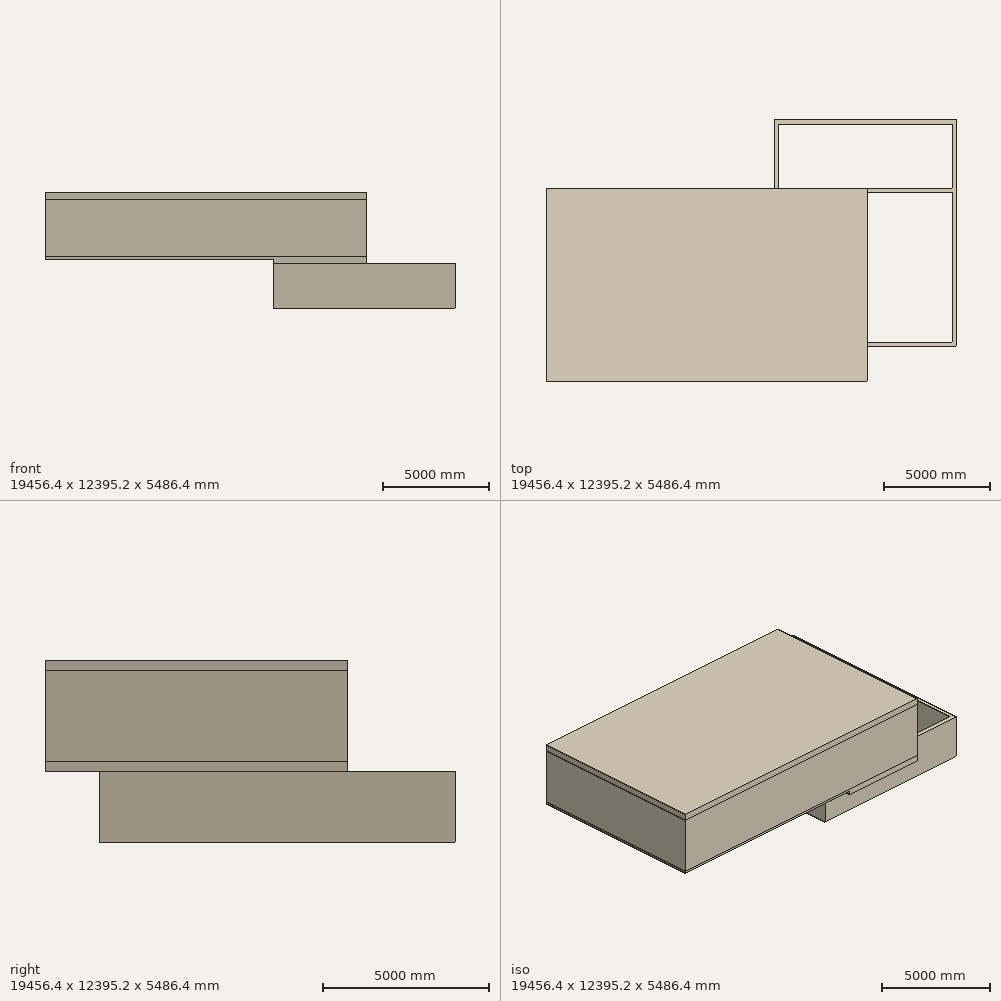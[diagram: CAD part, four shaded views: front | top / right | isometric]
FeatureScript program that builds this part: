
annotation { "Feature Type Name" : "Feature", "Feature Type Description" : "" }
export const myFeature = defineFeature(function(context is Context, id is Id, definition is map)
    precondition{}
    {
        {
            var Q0;
            Q0=qCreatedBy(makeId("Top.planeOp"),FACE);
            var sketch = newSketch(context, id + "F0", { "sketchPlane" : qUnion([Q0])});
            skLineSegment(sketch, "E0.bottom", {"start": v(4318, -5384.8) * mm, "end": v(-4318, -5384.8) * mm});
            skLineSegment(sketch, "E0.top", {"start": v(4318, 5384.8) * mm, "end": v(-4318, 5384.8) * mm});
            skLineSegment(sketch, "E0.left", {"start": v(4318, -5384.8) * mm, "end": v(4318, 5384.8) * mm});
            skLineSegment(sketch, "E0.right", {"start": v(-4318, -5384.8) * mm, "end": v(-4318, 5384.8) * mm});
            skPoint(sketch, "E0.middle", {"position": v(0, 0) * mm});
            skLineSegment(sketch, "E1.bottom", {"start": v(4114.8, -5181.6) * mm, "end": v(-4114.8, -5181.6) * mm});
            skLineSegment(sketch, "E1.top", {"start": v(4114.8, 5181.6) * mm, "end": v(-4114.8, 5181.6) * mm});
            skLineSegment(sketch, "E1.left", {"start": v(4114.8, -5181.6) * mm, "end": v(4114.8, 5181.6) * mm});
            skLineSegment(sketch, "E1.right", {"start": v(-4114.8, -5181.6) * mm, "end": v(-4114.8, 5181.6) * mm});
            skLineSegment(sketch, "E2.bottom", {"start": v(-4114.8, 2133.6) * mm, "end": v(1168.4, 2133.6) * mm});
            skLineSegment(sketch, "E2.top", {"start": v(-4114.8, 1930.4) * mm, "end": v(1168.4, 1930.4) * mm});
            skLineSegment(sketch, "E2.left", {"start": v(-4114.8, 2133.6) * mm, "end": v(-4114.8, 1930.4) * mm});
            skLineSegment(sketch, "E2.right", {"start": v(1168.4, 2133.6) * mm, "end": v(1168.4, 1930.4) * mm});
            skLineSegment(sketch, "E3.bottom", {"start": v(4114.8, 2133.6) * mm, "end": v(3302, 2133.6) * mm});
            skLineSegment(sketch, "E3.top", {"start": v(4114.8, 1930.4) * mm, "end": v(3302, 1930.4) * mm});
            skLineSegment(sketch, "E3.left", {"start": v(4114.8, 2133.6) * mm, "end": v(4114.8, 1930.4) * mm});
            skLineSegment(sketch, "E3.right", {"start": v(3302, 2133.6) * mm, "end": v(3302, 1930.4) * mm});
            skLineSegment(sketch, "E4.bottom", {"start": v(101.6, 1930.4) * mm, "end": v(-101.6, 1930.4) * mm});
            skLineSegment(sketch, "E4.top", {"start": v(101.6, -5181.6) * mm, "end": v(-101.6, -5181.6) * mm});
            skLineSegment(sketch, "E4.left", {"start": v(101.6, 1930.4) * mm, "end": v(101.6, -5181.6) * mm});
            skLineSegment(sketch, "E4.right", {"start": v(-101.6, 1930.4) * mm, "end": v(-101.6, -5181.6) * mm});
            skSolve(sketch);
        }
        {
            var Q0;
            Q0=makeQuery(id+"F0.imprint","IMPRINT",FACE,{"disambiguationData":[TD([[makeQuery(id+"F0.imprint","IMPRINT",EDGE,{"derivedFrom":sQuery(id+"F0.wireOp",EDGE,"E0.bottom")}),-1.0]])]});
            var Q1;
            {var subQ6=sQuery(id+"F0.wireOp",EDGE,"E2.bottom");Q1=makeQuery(id+"F0.imprint","IMPRINT",FACE,{"disambiguationData":[TD([[makeQuery(id+"F0.imprint","IMPRINT",EDGE,{"derivedFrom":subQ6}),-1.0]])]});}
            var Q2;
            {var subQ2=sQuery(id+"F0.wireOp",EDGE,"E4.left");Q2=makeQuery(id+"F0.imprint","IMPRINT",FACE,{"disambiguationData":[TD([[makeQuery(id+"F0.imprint","IMPRINT",EDGE,{"derivedFrom":subQ2}),-1.0]])]});}
            var Q3;
            {var subQ0=sQuery(id+"F0.wireOp",EDGE,"E3.bottom");Q3=makeQuery(id+"F0.imprint","IMPRINT",FACE,{"disambiguationData":[TD([[makeQuery(id+"F0.imprint","IMPRINT",EDGE,{"derivedFrom":subQ0}),1.0]])]});}
            extrude(context, id + "F1", {"entities" : qUnion([Q0, Q1, Q2, Q3]), "depth" : 2133.6 * mm, "offsetDistance" : 30.48 * mm});
        }
        {
            var Q0;
            {var subQ0=sQuery(id+"F0.wireOp",EDGE,"E2.top");Q0=makeQuery(id+"F1.opExtrude","SWEPT_FACE",FACE,{"disambiguationData":[OSD([subQ0]),TDD([makeQuery(id+"F0.imprint","IMPRINT",EDGE,{"disambiguationData":[TD([[makeQuery(id+"F0.imprint","INTERSECT",VERTEX,{"derivedFrom":[subQ0,sQuery(id+"F0.wireOp",EDGE,"E4.left")]}),-1.0]])],"derivedFrom":subQ0})])]});}
            var sketch = newSketch(context, id + "F2", { "sketchPlane" : qUnion([Q0])});
            skLineSegment(sketch, "E5", {"start": v(1168.4, 1930.4) * mm, "end": v(3302, 1930.4) * mm, "construction": true});
            skLineSegment(sketch, "E6", {"start": v(1168.4, 2133.6) * mm, "end": v(3302, 2133.6) * mm});
            skArc(sketch, "E7", {"start": v(2235.2, 1930.4) * mm, "mid": v(1548.93, 1687.44) * mm, "end": v(1168.4, 1066.8) * mm});
            skArc(sketch, "E8", {"start": v(3302, 1066.8) * mm, "mid": v(2921.47, 1687.44) * mm, "end": v(2235.2, 1930.4) * mm});
            skLineSegment(sketch, "E9", {"start": v(1168.4, 1066.8) * mm, "end": v(1168.4, 2133.6) * mm});
            skLineSegment(sketch, "E10", {"start": v(3302, 2133.6) * mm, "end": v(3302, 1066.8) * mm});
            skSolve(sketch);
        }
        {
            var Q0;
            Q0 = qSketchRegion(id + "F2", true);
            var Q1;
            Q1=makeQuery(id+"F1.opExtrude","SWEPT_FACE",FACE,{"disambiguationData":[OSD([sQuery(id+"F0.wireOp",EDGE,"E2.bottom")])]});
            extrude(context, id + "F3", {"entities" : qUnion([Q0]), "operationType" : NewBodyOperationType.ADD, "endBound" : BoundingType.UP_TO_SURFACE, "oppositeDirection" : true, "depth" : 30.48 * mm, "endBoundEntityFace" : qUnion([Q1]), "offsetDistance" : 30.48 * mm});
        }
        {
            var Q0;
            Q0=makeQuery(id+"F3.boolean.opBoolean","MERGE",FACE,{"derivedFrom":[makeQuery(id+"F1.opExtrude","CAP_FACE",FACE,{"disambiguationData":[OSD([sQuery(id+"F0.wireOp",EDGE,"E0.bottom"),sQuery(id+"F0.wireOp",EDGE,"E0.top"),sQuery(id+"F0.wireOp",EDGE,"E0.left"),sQuery(id+"F0.wireOp",EDGE,"E0.right"),sQuery(id+"F0.wireOp",EDGE,"E1.bottom"),sQuery(id+"F0.wireOp",EDGE,"E1.top"),sQuery(id+"F0.wireOp",EDGE,"E1.left"),sQuery(id+"F0.wireOp",EDGE,"E1.right"),sQuery(id+"F0.wireOp",EDGE,"E2.bottom"),sQuery(id+"F0.wireOp",EDGE,"E2.top"),sQuery(id+"F0.wireOp",EDGE,"E2.right"),sQuery(id+"F0.wireOp",EDGE,"E3.bottom"),sQuery(id+"F0.wireOp",EDGE,"E3.top"),sQuery(id+"F0.wireOp",EDGE,"E3.right"),sQuery(id+"F0.wireOp",EDGE,"E4.left"),sQuery(id+"F0.wireOp",EDGE,"E4.right")])],"isStart":false}),makeQuery(id+"F3.opExtrude","SWEPT_FACE",FACE,{"disambiguationData":[OSD([sQuery(id+"F2.wireOp",EDGE,"E6")])]})]});
            var sketch = newSketch(context, id + "F4", { "sketchPlane" : qUnion([Q0])});
            skLineSegment(sketch, "E11.bottom", {"start": v(101.6, -7010.4) * mm, "end": v(-4318, -7010.4) * mm});
            skLineSegment(sketch, "E11.top", {"start": v(101.6, 2133.6) * mm, "end": v(-4318, 2133.6) * mm});
            skLineSegment(sketch, "E11.left", {"start": v(101.6, -7010.4) * mm, "end": v(101.6, 2133.6) * mm});
            skLineSegment(sketch, "E11.right", {"start": v(-4318, -7010.4) * mm, "end": v(-4318, 2133.6) * mm});
            skSolve(sketch);
        }
        {
            var Q0;
            Q0 = qSketchRegion(id + "F4", true);
            extrude(context, id + "F5", {"entities" : qUnion([Q0]), "depth" : 304.8 * mm, "offsetDistance" : 30.48 * mm});
        }
        {
            var Q0;
            Q0=makeQuery(id+"F5.opExtrude","CAP_FACE",FACE,{"disambiguationData":[OSD([sQuery(id+"F4.wireOp",EDGE,"E11.bottom"),sQuery(id+"F4.wireOp",EDGE,"E11.top"),sQuery(id+"F4.wireOp",EDGE,"E11.left"),sQuery(id+"F4.wireOp",EDGE,"E11.right")])],"isStart":false});
            var sketch = newSketch(context, id + "F6", { "sketchPlane" : qUnion([Q0])});
            skLineSegment(sketch, "E12.bottom", {"start": v(-4318, -7010.4) * mm, "end": v(-15138.4, -7010.4) * mm});
            skLineSegment(sketch, "E12.top", {"start": v(-4318, 2133.6) * mm, "end": v(-15138.4, 2133.6) * mm});
            skLineSegment(sketch, "E12.left", {"start": v(-4318, -7010.4) * mm, "end": v(-4318, 2133.6) * mm});
            skLineSegment(sketch, "E12.right", {"start": v(-15138.4, -7010.4) * mm, "end": v(-15138.4, 2133.6) * mm});
            skSolve(sketch);
        }
        {
            var Q0;
            Q0 = qSketchRegion(id + "F6", true);
            var Q1;
            Q1=makeQuery(id+"F6.imprint","IMPRINT",FACE,{"disambiguationData":[TD([[makeQuery(id+"F6.imprint","IMPRINT",EDGE,{"derivedFrom":sQuery(id+"F6.wireOp",EDGE,"E12.left")}),-1.0]])]});
            extrude(context, id + "F7", {"entities" : qUnion([Q0, Q1]), "operationType" : NewBodyOperationType.ADD, "oppositeDirection" : true, "depth" : 127 * mm, "offsetDistance" : 30.48 * mm});
        }
        {
            var Q0;
            {var subQ0=sQuery(id+"F4.wireOp",EDGE,"E11.left");var subQ1=sQuery(id+"F4.wireOp",EDGE,"E11.top");var subQ2=sQuery(id+"F4.wireOp",EDGE,"E11.bottom");Q0=makeQuery(id+"F7.boolean.opBoolean","MERGE",FACE,{"derivedFrom":[makeQuery(id+"F5.opExtrude","CAP_FACE",FACE,{"disambiguationData":[OSD([subQ2,subQ1,subQ0,sQuery(id+"F4.wireOp",EDGE,"E11.right")])],"isStart":false}),makeQuery(id+"F7.opExtrude","CAP_FACE",FACE,{"disambiguationData":[OSD([subQ2,subQ1,subQ0,sQuery(id+"F6.wireOp",EDGE,"E12.bottom"),sQuery(id+"F6.wireOp",EDGE,"E12.top"),sQuery(id+"F6.wireOp",EDGE,"E12.right")])],"isStart":true})]});}
            var sketch = newSketch(context, id + "F8", { "sketchPlane" : qUnion([Q0])});
            skLineSegment(sketch, "E13.bottom", {"start": v(101.6, 2133.6) * mm, "end": v(-15138.4, 2133.6) * mm});
            skLineSegment(sketch, "E13.top", {"start": v(101.6, -7010.4) * mm, "end": v(-15138.4, -7010.4) * mm});
            skLineSegment(sketch, "E13.left", {"start": v(101.6, 2133.6) * mm, "end": v(101.6, -7010.4) * mm});
            skLineSegment(sketch, "E13.right", {"start": v(-15138.4, 2133.6) * mm, "end": v(-15138.4, -7010.4) * mm});
            skLineSegment(sketch, "E14.bottom", {"start": v(-101.6, 1930.4) * mm, "end": v(-14935.2, 1930.4) * mm});
            skLineSegment(sketch, "E14.top", {"start": v(-101.6, -6807.2) * mm, "end": v(-14935.2, -6807.2) * mm});
            skLineSegment(sketch, "E14.left", {"start": v(-101.6, 1930.4) * mm, "end": v(-101.6, -6807.2) * mm});
            skLineSegment(sketch, "E14.right", {"start": v(-14935.2, 1930.4) * mm, "end": v(-14935.2, -6807.2) * mm});
            skLineSegment(sketch, "E15.left", {"start": v(101.6, -1586.05) * mm, "end": v(101.6, -1312.76) * mm});
            skLineSegment(sketch, "E15.right", {"start": v(-101.6, -1586.05) * mm, "end": v(-101.6, -1312.76) * mm});
            skSolve(sketch);
        }
        {
            var Q0;
            Q0 = qSketchRegion(id + "F8", true);
            extrude(context, id + "F9", {"entities" : qUnion([Q0]), "depth" : 2743.2 * mm, "offsetDistance" : 30.48 * mm});
        }
        {
            var Q0;
            Q0=makeQuery(id+"F9.opExtrude","CAP_FACE",FACE,{"disambiguationData":[OSD([sQuery(id+"F8.wireOp",EDGE,"E13.bottom"),sQuery(id+"F8.wireOp",EDGE,"E13.top"),sQuery(id+"F8.wireOp",EDGE,"E13.left"),sQuery(id+"F8.wireOp",EDGE,"E13.right"),sQuery(id+"F8.wireOp",EDGE,"E14.bottom"),sQuery(id+"F8.wireOp",EDGE,"E14.top"),sQuery(id+"F8.wireOp",EDGE,"E14.left"),sQuery(id+"F8.wireOp",EDGE,"E14.right"),sQuery(id+"F8.wireOp",EDGE,"E15.left"),sQuery(id+"F8.wireOp",EDGE,"E15.right")])],"isStart":false});
            var sketch = newSketch(context, id + "F10", { "sketchPlane" : qUnion([Q0])});
            skLineSegment(sketch, "E16.bottom", {"start": v(101.6, 2133.6) * mm, "end": v(-15138.4, 2133.6) * mm});
            skLineSegment(sketch, "E16.top", {"start": v(101.6, -7010.4) * mm, "end": v(-15138.4, -7010.4) * mm});
            skLineSegment(sketch, "E16.left", {"start": v(101.6, 2133.6) * mm, "end": v(101.6, -7010.4) * mm});
            skLineSegment(sketch, "E16.right", {"start": v(-15138.4, 2133.6) * mm, "end": v(-15138.4, -7010.4) * mm});
            skSolve(sketch);
        }
        {
            var Q0;
            Q0 = qSketchRegion(id + "F10", true);
            extrude(context, id + "F11", {"entities" : qUnion([Q0]), "depth" : 304.8 * mm, "offsetDistance" : 30.48 * mm});
        }
    });
